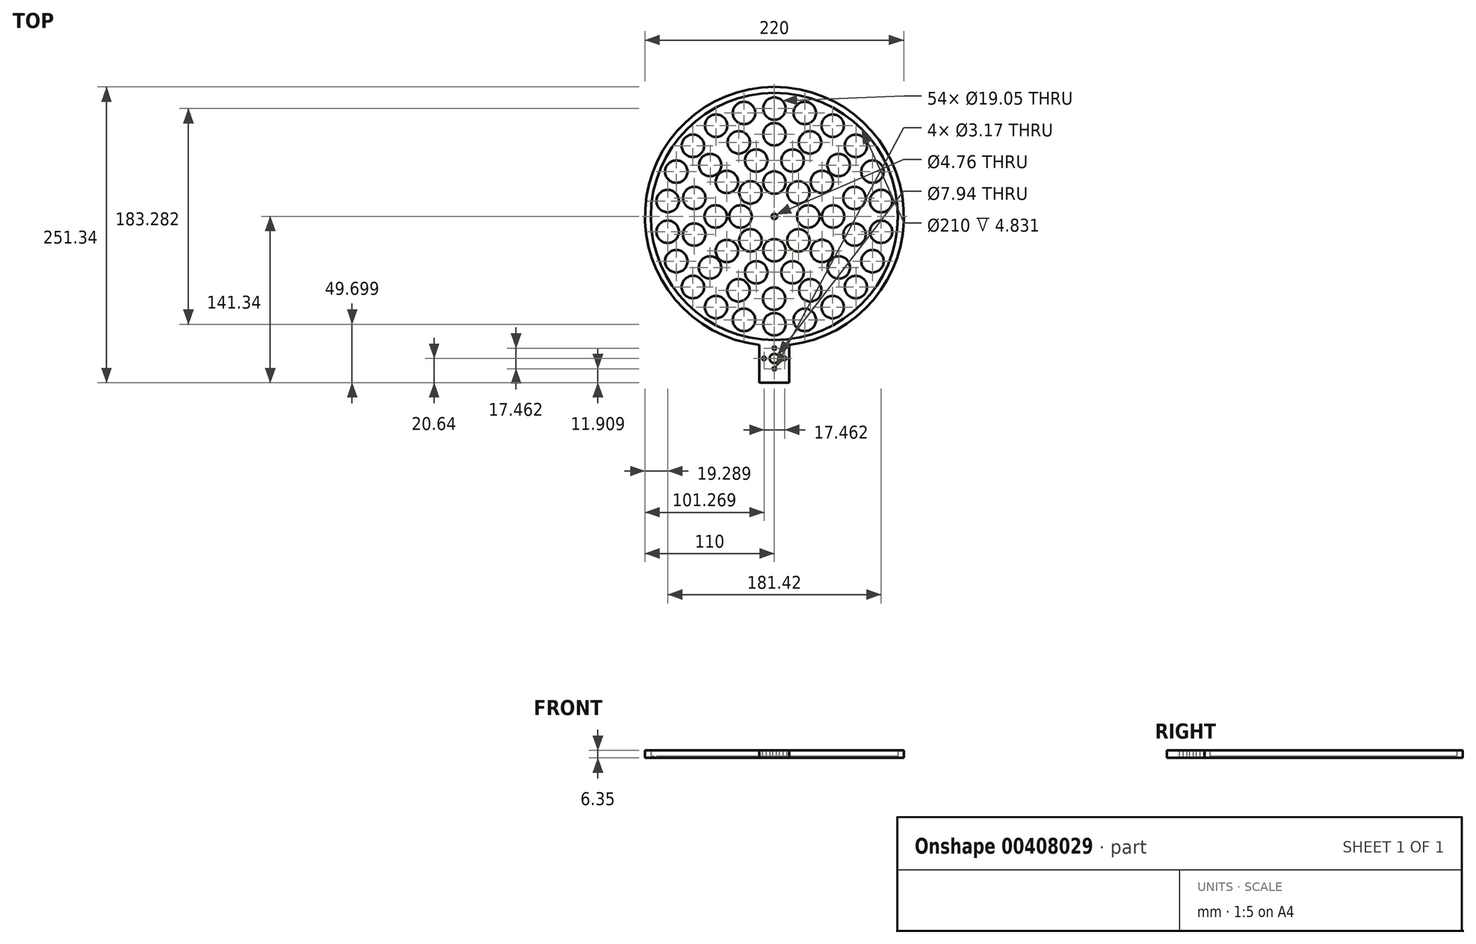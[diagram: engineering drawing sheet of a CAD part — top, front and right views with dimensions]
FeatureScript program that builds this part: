
annotation { "Feature Type Name" : "Feature", "Feature Type Description" : "" }
export const myFeature = defineFeature(function(context is Context, id is Id, definition is map)
    precondition{}
    {
        {
            var Q0;
            Q0=qCreatedBy(makeId("Top.planeOp"),FACE);
            var sketch = newSketch(context, id + "F0", { "sketchPlane" : qUnion([Q0])});
            skCircle(sketch, "E0", {"center": v(0, 0) * mm, "radius": 110 * mm});
            skCircle(sketch, "E1", {"center": v(0, 0) * mm, "radius": 40 * mm, "construction": true});
            skCircle(sketch, "E2", {"center": v(0, 28.8) * mm, "radius": 9.53 * mm});
            skCircle(sketch, "E3", {"center": v(54.73, -43.4) * mm, "radius": 9.53 * mm});
            skCircle(sketch, "E4", {"center": v(-69.27, -60) * mm, "radius": 9.53 * mm});
            skCircle(sketch, "E5", {"center": v(-83.37, -38.05) * mm, "radius": 9.53 * mm});
            skCircle(sketch, "E6", {"center": v(-30.52, -62.83) * mm, "radius": 9.53 * mm});
            skCircle(sketch, "E7", {"center": v(-49.56, -77.08) * mm, "radius": 9.53 * mm});
            skCircle(sketch, "E8", {"center": v(-25.8, 87.93) * mm, "radius": 9.53 * mm});
            skCircle(sketch, "E9", {"center": v(49.55, 77.09) * mm, "radius": 9.53 * mm});
            skCircle(sketch, "E10", {"center": v(-0.27, -69.85) * mm, "radius": 9.53 * mm});
            skCircle(sketch, "E11", {"center": v(30.52, -62.83) * mm, "radius": 9.53 * mm});
            skCircle(sketch, "E12", {"center": v(90.7, -13.05) * mm, "radius": 9.53 * mm});
            skCircle(sketch, "E13", {"center": v(90.7, 13.04) * mm, "radius": 9.53 * mm});
            skCircle(sketch, "E14", {"center": v(20.36, 20.36) * mm, "radius": 9.53 * mm});
            skCircle(sketch, "E15", {"center": v(-90.71, -13.03) * mm, "radius": 9.53 * mm});
            skCircle(sketch, "E16", {"center": v(-90.7, 13.06) * mm, "radius": 9.53 * mm});
            skCircle(sketch, "E17", {"center": v(-83.35, 38.08) * mm, "radius": 9.53 * mm});
            skCircle(sketch, "E18", {"center": v(69.26, 60) * mm, "radius": 9.53 * mm});
            skCircle(sketch, "E19", {"center": v(83.36, 38.06) * mm, "radius": 9.53 * mm});
            skCircle(sketch, "E20", {"center": v(-54.73, -43.4) * mm, "radius": 9.53 * mm});
            skCircle(sketch, "E21", {"center": v(-49.53, 77.1) * mm, "radius": 9.53 * mm});
            skCircle(sketch, "E22", {"center": v(-69.25, 60.02) * mm, "radius": 9.53 * mm});
            skCircle(sketch, "E23", {"center": v(25.83, 87.93) * mm, "radius": 9.53 * mm});
            skCircle(sketch, "E24", {"center": v(-28.8, 0) * mm, "radius": 9.53 * mm});
            skCircle(sketch, "E25", {"center": v(20.36, -20.36) * mm, "radius": 9.53 * mm});
            skCircle(sketch, "E26", {"center": v(-20.36, -20.36) * mm, "radius": 9.53 * mm});
            skCircle(sketch, "E27", {"center": v(-20.36, 20.36) * mm, "radius": 9.53 * mm});
            skCircle(sketch, "E28", {"center": v(0.01, 91.64) * mm, "radius": 9.53 * mm});
            skCircle(sketch, "E29", {"center": v(54.56, 43.61) * mm, "radius": 9.53 * mm});
            skCircle(sketch, "E30", {"center": v(0, 69.85) * mm, "radius": 9.53 * mm});
            skCircle(sketch, "E31", {"center": v(68.13, -15.4) * mm, "radius": 9.53 * mm});
            skCircle(sketch, "E32", {"center": v(68.07, 15.66) * mm, "radius": 9.53 * mm});
            skCircle(sketch, "E33", {"center": v(30.27, 62.95) * mm, "radius": 9.53 * mm});
            skCircle(sketch, "E34", {"center": v(0, -28.8) * mm, "radius": 9.53 * mm});
            skCircle(sketch, "E35", {"center": v(28.8, 0) * mm, "radius": 9.53 * mm});
            skCircle(sketch, "E36", {"center": v(0, 0) * mm, "radius": 2.38 * mm});
            skCircle(sketch, "E37", {"center": v(0, 0) * mm, "radius": 28.8 * mm, "construction": true});
            skCircle(sketch, "E38", {"center": v(0, 0) * mm, "radius": 69.85 * mm, "construction": true});
            skCircle(sketch, "E39", {"center": v(0, 0) * mm, "radius": 91.64 * mm, "construction": true});
            skCircle(sketch, "E40", {"center": v(0, 0) * mm, "radius": 80 * mm, "construction": true});
            skCircle(sketch, "E41", {"center": v(83.36, -38.07) * mm, "radius": 9.53 * mm});
            skCircle(sketch, "E42", {"center": v(69.26, -60.01) * mm, "radius": 9.53 * mm});
            skCircle(sketch, "E43", {"center": v(0, 0) * mm, "radius": 105 * mm});
            skCircle(sketch, "E44", {"center": v(40.38, 29.33) * mm, "radius": 9.53 * mm});
            skCircle(sketch, "E45", {"center": v(49.91, 0) * mm, "radius": 9.53 * mm});
            skCircle(sketch, "E46", {"center": v(-15.41, -47.47) * mm, "radius": 9.53 * mm});
            skCircle(sketch, "E47", {"center": v(-49.91, -0.02) * mm, "radius": 9.53 * mm});
            skCircle(sketch, "E48", {"center": v(-40.4, 29.32) * mm, "radius": 9.53 * mm});
            skCircle(sketch, "E49", {"center": v(15.43, -47.47) * mm, "radius": 9.53 * mm});
            skCircle(sketch, "E50", {"center": v(40.38, -29.33) * mm, "radius": 9.53 * mm});
            skCircle(sketch, "E51", {"center": v(-15.45, 47.46) * mm, "radius": 9.53 * mm});
            skCircle(sketch, "E52", {"center": v(15.43, 47.47) * mm, "radius": 9.53 * mm});
            skCircle(sketch, "E53", {"center": v(0, 0) * mm, "radius": 49.91 * mm, "construction": true});
            skCircle(sketch, "E54", {"center": v(-40.37, -29.35) * mm, "radius": 9.53 * mm});
            skCircle(sketch, "E55", {"center": v(-30.27, 62.95) * mm, "radius": 9.53 * mm});
            skCircle(sketch, "E56", {"center": v(-68.13, -15.4) * mm, "radius": 9.53 * mm});
            skCircle(sketch, "E57", {"center": v(-25.82, -87.93) * mm, "radius": 9.53 * mm});
            skCircle(sketch, "E58", {"center": v(-54.56, 43.61) * mm, "radius": 9.53 * mm});
            skCircle(sketch, "E59", {"center": v(-68.07, 15.66) * mm, "radius": 9.53 * mm});
            skCircle(sketch, "E60", {"center": v(0, -91.64) * mm, "radius": 9.53 * mm});
            skCircle(sketch, "E61", {"center": v(25.82, -87.93) * mm, "radius": 9.53 * mm});
            skCircle(sketch, "E62", {"center": v(49.54, -77.1) * mm, "radius": 9.53 * mm});
            skCircle(sketch, "E63", {"center": v(0, 0) * mm, "radius": 108 * mm, "construction": true});
            skLineSegment(sketch, "E64.bottom", {"start": v(-12.7, -108) * mm, "end": v(12.7, -108) * mm});
            skLineSegment(sketch, "E64.top", {"start": v(-12.7, -141.34) * mm, "end": v(12.7, -141.34) * mm});
            skLineSegment(sketch, "E64.left", {"start": v(-12.7, -108) * mm, "end": v(-12.7, -141.34) * mm});
            skLineSegment(sketch, "E64.right", {"start": v(12.7, -108) * mm, "end": v(12.7, -141.34) * mm});
            skPoint(sketch, "E65", {"position": v(0, -108) * mm});
            skCircle(sketch, "E66", {"center": v(0, -111.97) * mm, "radius": 1.59 * mm});
            skCircle(sketch, "E67", {"center": v(-8.73, -120.7) * mm, "radius": 1.59 * mm});
            skCircle(sketch, "E68", {"center": v(8.73, -120.7) * mm, "radius": 1.59 * mm});
            skCircle(sketch, "E69", {"center": v(0, -129.43) * mm, "radius": 1.59 * mm});
            skCircle(sketch, "E70", {"center": v(0, -120.7) * mm, "radius": 3.97 * mm});
            skSolve(sketch);
        }
        {
            var Q0;
            Q0=makeQuery(id+"F0.imprint","IMPRINT",FACE,{"disambiguationData":[TD([[makeQuery(id+"F0.imprint","IMPRINT",EDGE,{"derivedFrom":sQuery(id+"F0.wireOp",EDGE,"E2")}),-1.0]])]});
            extrude(context, id + "F1", {"entities" : qUnion([Q0]), "depth" : 1.52 * mm, "offsetDistance" : 25.4 * mm});
        }
        {
            var Q0;
            Q0=makeQuery(id+"F0.imprint","IMPRINT",FACE,{"disambiguationData":[TD([[makeQuery(id+"F0.imprint","IMPRINT",EDGE,{"derivedFrom":sQuery(id+"F0.wireOp",EDGE,"E0")}),1.0]])]});
            var Q1;
            Q1=makeQuery(id+"F0.imprint","IMPRINT",FACE,{"disambiguationData":[TD([[makeQuery(id+"F0.imprint","IMPRINT",EDGE,{"derivedFrom":sQuery(id+"F0.wireOp",EDGE,"E43")}),-1.0]])]});
            var Q2;
            {var subQ1=sQuery(id+"F0.wireOp",EDGE,"E64.top");Q2=makeQuery(id+"F0.imprint","IMPRINT",FACE,{"disambiguationData":[TD([[makeQuery(id+"F0.imprint","IMPRINT",EDGE,{"derivedFrom":subQ1}),1.0]])]});}
            extrude(context, id + "F2", {"entities" : qUnion([Q0, Q1, Q2]), "operationType" : NewBodyOperationType.ADD, "depth" : 6.35 * mm, "offsetDistance" : 25.4 * mm});
        }
    });
